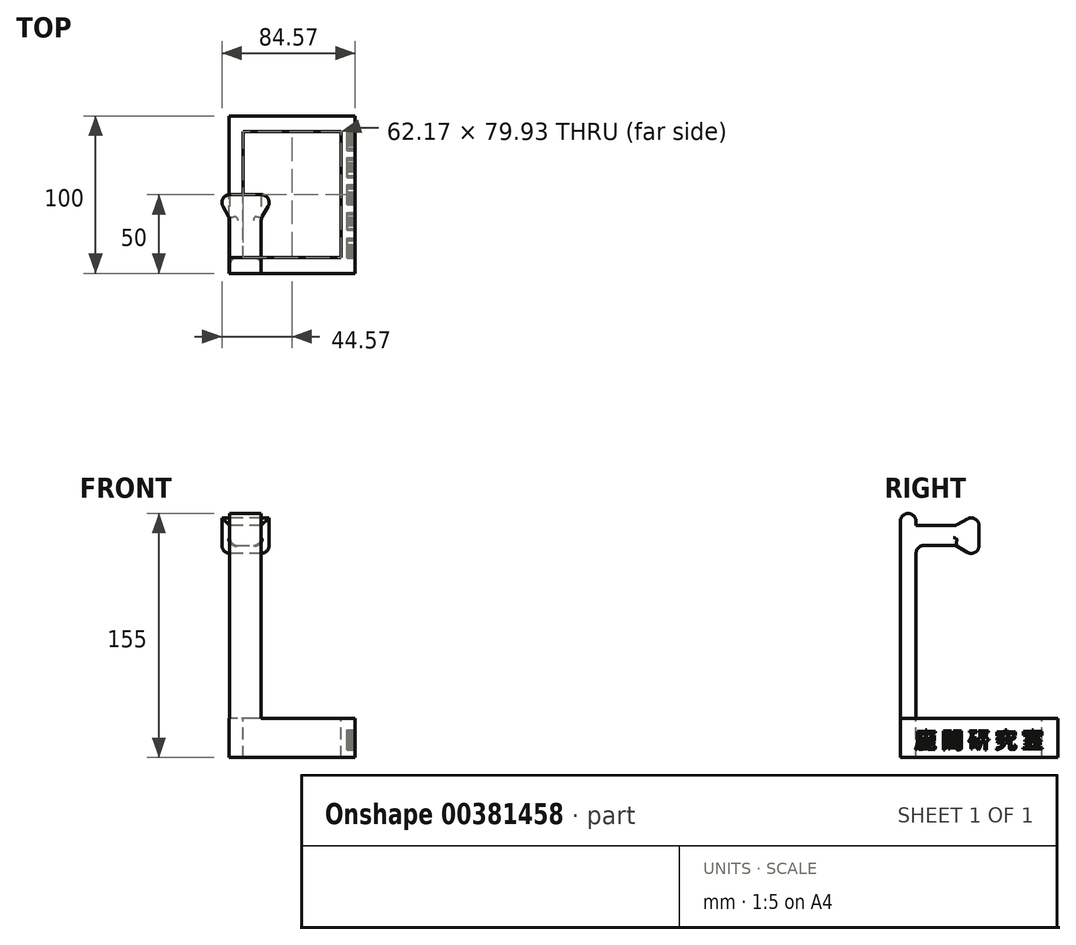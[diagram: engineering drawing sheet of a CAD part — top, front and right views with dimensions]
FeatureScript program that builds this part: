
annotation { "Feature Type Name" : "Feature", "Feature Type Description" : "" }
export const myFeature = defineFeature(function(context is Context, id is Id, definition is map)
    precondition{}
    {
        {
            var Q0;
            Q0=qCreatedBy(makeId("Top.planeOp"),FACE);
            var sketch = newSketch(context, id + "F0", { "sketchPlane" : qUnion([Q0])});
            skLineSegment(sketch, "E0.bottom", {"start": v(40, -50) * mm, "end": v(-40, -50) * mm});
            skLineSegment(sketch, "E0.top", {"start": v(40, 50) * mm, "end": v(-40, 50) * mm});
            skLineSegment(sketch, "E0.left", {"start": v(40, -50) * mm, "end": v(40, 50) * mm});
            skLineSegment(sketch, "E0.right", {"start": v(-40, -50) * mm, "end": v(-40, 50) * mm});
            skPoint(sketch, "E0.middle", {"position": v(0, 0) * mm});
            skSolve(sketch);
        }
        {
            var Q0;
            Q0=makeQuery(id+"F0.imprint","IMPRINT",FACE,{"disambiguationData":[TD([[makeQuery(id+"F0.imprint","IMPRINT",EDGE,{"derivedFrom":sQuery(id+"F0.wireOp",EDGE,"E0.bottom")}),-1.0]])]});
            extrude(context, id + "F1", {"entities" : qUnion([Q0]), "depth" : 25 * mm});
        }
        {
            var Q0;
            Q0=makeQuery(id+"F1.opExtrude","CAP_FACE",FACE,{"disambiguationData":[OSD([sQuery(id+"F0.wireOp",EDGE,"E0.bottom"),sQuery(id+"F0.wireOp",EDGE,"E0.top"),sQuery(id+"F0.wireOp",EDGE,"E0.left"),sQuery(id+"F0.wireOp",EDGE,"E0.right")])],"isStart":false});
            var sketch = newSketch(context, id + "F2", { "sketchPlane" : qUnion([Q0])});
            skLineSegment(sketch, "E1.bottom", {"start": v(-19.57, -50) * mm, "end": v(-39.57, -50) * mm});
            skLineSegment(sketch, "E1.top", {"start": v(-19.57, -40) * mm, "end": v(-39.57, -40) * mm});
            skLineSegment(sketch, "E1.left", {"start": v(-19.57, -50) * mm, "end": v(-19.57, -40) * mm});
            skLineSegment(sketch, "E1.right", {"start": v(-39.57, -50) * mm, "end": v(-39.57, -40) * mm});
            skPoint(sketch, "E1.middle", {"position": v(-29.57, -45) * mm});
            skSolve(sketch);
        }
        {
            var Q0;
            Q0=makeQuery(id+"F2.imprint","IMPRINT",FACE,{"disambiguationData":[TD([[makeQuery(id+"F2.imprint","IMPRINT",EDGE,{"derivedFrom":sQuery(id+"F2.wireOp",EDGE,"E1.bottom")}),-1.0]])]});
            extrude(context, id + "F3", {"entities" : qUnion([Q0]), "operationType" : NewBodyOperationType.ADD, "depth" : 130 * mm});
        }
        {
            var Q0;
            Q0=makeQuery(id+"F1.opExtrude","SWEPT_FACE",FACE,{"disambiguationData":[OSD([sQuery(id+"F0.wireOp",EDGE,"E0.left")])]});
            var sketch = newSketch(context, id + "F4", { "sketchPlane" : qUnion([Q0])});
            skText(sketch, "E2", { "text": "鹿 間 研 究 室", "fontName": "NotoSansCJKjp-Regular.otf"});
            const initialGuessF4  = {"E2": [-0.04089, 0.006, 1, 0, 0.01]};
            skSetInitialGuess(sketch, initialGuessF4);
            skSolve(sketch);
        }
        {
            var Q0;
            Q0 = qSketchRegion(id + "F4", true);
            extrude(context, id + "F5", {"entities" : qUnion([Q0]), "operationType" : NewBodyOperationType.REMOVE, "oppositeDirection" : true, "depth" : 5 * mm});
        }
        {
            var Q0;
            Q0=makeQuery(id+"F2.imprint","IMPRINT",FACE,{"disambiguationData":[TD([[makeQuery(id+"F2.imprint","IMPRINT",EDGE,{"derivedFrom":sQuery(id+"F2.wireOp",EDGE,"E1.top")}),-1.0]])]});
            var sketch = newSketch(context, id + "F6", { "sketchPlane" : qUnion([Q0])});
            skLineSegment(sketch, "E3.bottom", {"start": v(31.09, -39.97) * mm, "end": v(-31.09, -39.97) * mm});
            skLineSegment(sketch, "E3.top", {"start": v(31.09, 39.97) * mm, "end": v(-31.09, 39.97) * mm});
            skLineSegment(sketch, "E3.left", {"start": v(31.09, -39.97) * mm, "end": v(31.09, 39.97) * mm});
            skLineSegment(sketch, "E3.right", {"start": v(-31.09, -39.97) * mm, "end": v(-31.09, 39.97) * mm});
            skPoint(sketch, "E3.middle", {"position": v(0, 0) * mm});
            skSolve(sketch);
        }
        {
            var Q0;
            Q0 = qSketchRegion(id + "F6", true);
            extrude(context, id + "F7", {"entities" : qUnion([Q0]), "operationType" : NewBodyOperationType.REMOVE, "endBound" : BoundingType.THROUGH_ALL, "oppositeDirection" : true, "depth" : 25 * mm});
        }
        {
            var Q0;
            Q0=makeQuery(id+"F3.opExtrude","SWEPT_FACE",FACE,{"disambiguationData":[OSD([sQuery(id+"F2.wireOp",EDGE,"E1.top")])]});
            var sketch = newSketch(context, id + "F8", { "sketchPlane" : qUnion([Q0])});
            skLineSegment(sketch, "E4.bottom", {"start": v(19.57, 147.26) * mm, "end": v(39.57, 147.26) * mm});
            skLineSegment(sketch, "E4.top", {"start": v(19.57, 134.68) * mm, "end": v(39.57, 134.68) * mm});
            skLineSegment(sketch, "E4.left", {"start": v(19.57, 147.26) * mm, "end": v(19.57, 134.68) * mm});
            skLineSegment(sketch, "E4.right", {"start": v(39.57, 147.26) * mm, "end": v(39.57, 134.68) * mm});
            skSolve(sketch);
        }
        {
            var Q0;
            Q0=makeQuery(id+"F8.imprint","IMPRINT",FACE,{"disambiguationData":[TD([[makeQuery(id+"F8.imprint","IMPRINT",EDGE,{"derivedFrom":sQuery(id+"F8.wireOp",EDGE,"E4.bottom")}),-1.0]])]});
            extrude(context, id + "F9", {"entities" : qUnion([Q0]), "operationType" : NewBodyOperationType.ADD, "depth" : 25 * mm});
        }
        {
            var Q0;
            Q0=makeQuery(id+"F9.opExtrude","CAP_FACE",FACE,{"disambiguationData":[OSD([sQuery(id+"F8.wireOp",EDGE,"E4.bottom"),sQuery(id+"F8.wireOp",EDGE,"E4.top"),sQuery(id+"F8.wireOp",EDGE,"E4.left"),sQuery(id+"F8.wireOp",EDGE,"E4.right")])],"isStart":false});
            extrude(context, id + "F10", {"entities" : qUnion([Q0]), "operationType" : NewBodyOperationType.ADD, "depth" : 10 * mm, "hasDraft" : true, "draftAngle" : 30 * degree});
        }
        {
            var Q0;
            Q0=makeQuery(id+"F10.opExtrude","CAP_FACE",FACE,{"disambiguationData":[OSD([sQuery(id+"F8.wireOp",EDGE,"E4.bottom"),sQuery(id+"F8.wireOp",EDGE,"E4.top"),sQuery(id+"F8.wireOp",EDGE,"E4.left"),sQuery(id+"F8.wireOp",EDGE,"E4.right")])],"isStart":false});
            extrude(context, id + "F11", {"entities" : qUnion([Q0]), "operationType" : NewBodyOperationType.ADD, "depth" : 5 * mm});
        }
        {
            var Q0;
            Q0=makeQuery(id+"F11.opExtrude","CAP_FACE",FACE,{"disambiguationData":[OSD([sQuery(id+"F8.wireOp",EDGE,"E4.bottom"),sQuery(id+"F8.wireOp",EDGE,"E4.top"),sQuery(id+"F8.wireOp",EDGE,"E4.left"),sQuery(id+"F8.wireOp",EDGE,"E4.right")])],"isStart":false});
            fillet(context, id + "F12", {"entities" : qUnion([Q0]), "radius" : 5 * mm, "tangentPropagation" : true, "allowEdgeOverflow" : false});
        }
        {
            var Q0;
            {var subQ0=sQuery(id+"F8.wireOp",EDGE,"E4.bottom");Q0=makeQuery(id+"F10.boolean.opBoolean","MERGE",EDGE,{"derivedFrom":[makeQuery(id+"F9.opExtrude","CAP_EDGE",EDGE,{"disambiguationData":[OSD([subQ0])],"isStart":false}),makeQuery(id+"F10.opExtrude","CAP_EDGE",EDGE,{"disambiguationData":[OSD([subQ0])],"isStart":true})]});}
            var Q1;
            {var subQ0=sQuery(id+"F8.wireOp",EDGE,"E4.left");Q1=makeQuery(id+"F10.boolean.opBoolean","MERGE",EDGE,{"derivedFrom":[makeQuery(id+"F9.opExtrude","CAP_EDGE",EDGE,{"disambiguationData":[OSD([subQ0])],"isStart":false}),makeQuery(id+"F10.opExtrude","CAP_EDGE",EDGE,{"disambiguationData":[OSD([subQ0])],"isStart":true})]});}
            var Q2;
            {var subQ0=sQuery(id+"F8.wireOp",EDGE,"E4.top");Q2=makeQuery(id+"F10.boolean.opBoolean","MERGE",EDGE,{"derivedFrom":[makeQuery(id+"F9.opExtrude","CAP_EDGE",EDGE,{"disambiguationData":[OSD([subQ0])],"isStart":false}),makeQuery(id+"F10.opExtrude","CAP_EDGE",EDGE,{"disambiguationData":[OSD([subQ0])],"isStart":true})]});}
            var Q3;
            {var subQ0=sQuery(id+"F8.wireOp",EDGE,"E4.right");Q3=makeQuery(id+"F10.boolean.opBoolean","MERGE",EDGE,{"derivedFrom":[makeQuery(id+"F9.opExtrude","CAP_EDGE",EDGE,{"disambiguationData":[OSD([subQ0])],"isStart":false}),makeQuery(id+"F10.opExtrude","CAP_EDGE",EDGE,{"disambiguationData":[OSD([subQ0])],"isStart":true})]});}
            var Q4;
            Q4=makeQuery(id+"F9.opExtrude","CAP_EDGE",EDGE,{"disambiguationData":[OSD([sQuery(id+"F8.wireOp",EDGE,"E4.bottom")])],"isStart":true});
            var Q5;
            Q5=makeQuery(id+"F9.opExtrude","CAP_EDGE",EDGE,{"disambiguationData":[OSD([sQuery(id+"F8.wireOp",EDGE,"E4.top")])],"isStart":true});
            var Q6;
            Q6=makeQuery(id+"F3.opExtrude","CAP_EDGE",EDGE,{"disambiguationData":[OSD([sQuery(id+"F2.wireOp",EDGE,"E1.top")])],"isStart":false});
            var Q7;
            Q7=makeQuery(id+"F3.opExtrude","CAP_EDGE",EDGE,{"disambiguationData":[OSD([sQuery(id+"F2.wireOp",EDGE,"E1.bottom")])],"isStart":false});
            var Q8;
            {var subQ0=sQuery(id+"F8.wireOp",EDGE,"E4.bottom");Q8=makeQuery(id+"F12.opFillet","BLEND_EDGE",EDGE,{"blendedFrom":[makeQuery(id+"F11.opExtrude","CAP_EDGE",EDGE,{"disambiguationData":[OSD([subQ0])],"isStart":false}),makeQuery(id+"F10.opExtrude","SWEPT_FACE",FACE,{"disambiguationData":[OSD([subQ0])]})],"blendedInto":[makeQuery(id+"F10.opExtrude","SWEPT_FACE",FACE,{"disambiguationData":[OSD([subQ0])]})]});}
            var Q9;
            {var subQ0=sQuery(id+"F8.wireOp",EDGE,"E4.top");Q9=makeQuery(id+"F12.opFillet","BLEND_EDGE",EDGE,{"blendedFrom":[makeQuery(id+"F11.opExtrude","CAP_EDGE",EDGE,{"disambiguationData":[OSD([subQ0])],"isStart":false}),makeQuery(id+"F10.opExtrude","SWEPT_FACE",FACE,{"disambiguationData":[OSD([subQ0])]})],"blendedInto":[makeQuery(id+"F10.opExtrude","SWEPT_FACE",FACE,{"disambiguationData":[OSD([subQ0])]})]});}
            fillet(context, id + "F13", {"entities" : qUnion([Q0, Q1, Q2, Q3, Q4, Q5, Q6, Q7, Q8, Q9]), "radius" : 5 * mm, "tangentPropagation" : true, "allowEdgeOverflow" : false});
        }
        {
            var Q0;
            {var subQ0=sQuery(id+"F2.wireOp",EDGE,"E1.right");var subQ1=sQuery(id+"F2.wireOp",EDGE,"E1.top");Q0=makeQuery(id+"F9.boolean.opBoolean","SPLIT",EDGE,{"disambiguationData":[TD([makeQuery(id+"F9.opExtrude","SWEPT_FACE",FACE,{"disambiguationData":[OSD([sQuery(id+"F8.wireOp",EDGE,"E4.top")])]})])],"derivedFrom":makeQuery(id+"F3.opExtrude","SWEPT_EDGE",EDGE,{"disambiguationData":[OSD([subQ1,subQ0])]})});}
            var Q1;
            Q1=makeQuery(id+"F13.opFillet","BLEND_EDGE",EDGE,{"blendedFrom":[makeQuery(id+"F9.opExtrude","CAP_EDGE",EDGE,{"disambiguationData":[OSD([sQuery(id+"F8.wireOp",EDGE,"E4.bottom")])],"isStart":true}),makeQuery(id+"F9.boolean.opBoolean","MERGE",FACE,{"derivedFrom":[makeQuery(id+"F3.opExtrude","SWEPT_FACE",FACE,{"disambiguationData":[OSD([sQuery(id+"F2.wireOp",EDGE,"E1.right")])]}),makeQuery(id+"F9.opExtrude","SWEPT_FACE",FACE,{"disambiguationData":[OSD([sQuery(id+"F8.wireOp",EDGE,"E4.right")])]})]})],"blendedInto":[makeQuery(id+"F9.boolean.opBoolean","MERGE",FACE,{"derivedFrom":[makeQuery(id+"F3.opExtrude","SWEPT_FACE",FACE,{"disambiguationData":[OSD([sQuery(id+"F2.wireOp",EDGE,"E1.right")])]}),makeQuery(id+"F9.opExtrude","SWEPT_FACE",FACE,{"disambiguationData":[OSD([sQuery(id+"F8.wireOp",EDGE,"E4.right")])]})]})]});
            var Q2;
            Q2=makeQuery(id+"F13.opFillet","BLEND_EDGE",EDGE,{"blendedFrom":[makeQuery(id+"F9.opExtrude","CAP_EDGE",EDGE,{"disambiguationData":[OSD([sQuery(id+"F8.wireOp",EDGE,"E4.bottom")])],"isStart":true}),makeQuery(id+"F9.boolean.opBoolean","MERGE",FACE,{"derivedFrom":[makeQuery(id+"F3.opExtrude","SWEPT_FACE",FACE,{"disambiguationData":[OSD([sQuery(id+"F2.wireOp",EDGE,"E1.left")])]}),makeQuery(id+"F9.opExtrude","SWEPT_FACE",FACE,{"disambiguationData":[OSD([sQuery(id+"F8.wireOp",EDGE,"E4.left")])]})]})],"blendedInto":[makeQuery(id+"F9.boolean.opBoolean","MERGE",FACE,{"derivedFrom":[makeQuery(id+"F3.opExtrude","SWEPT_FACE",FACE,{"disambiguationData":[OSD([sQuery(id+"F2.wireOp",EDGE,"E1.left")])]}),makeQuery(id+"F9.opExtrude","SWEPT_FACE",FACE,{"disambiguationData":[OSD([sQuery(id+"F8.wireOp",EDGE,"E4.left")])]})]})]});
            var Q3;
            {var subQ0=sQuery(id+"F2.wireOp",EDGE,"E1.top");var subQ1=sQuery(id+"F2.wireOp",EDGE,"E1.left");Q3=makeQuery(id+"F9.boolean.opBoolean","SPLIT",EDGE,{"disambiguationData":[TD([makeQuery(id+"F9.opExtrude","SWEPT_FACE",FACE,{"disambiguationData":[OSD([sQuery(id+"F8.wireOp",EDGE,"E4.top")])]})])],"derivedFrom":makeQuery(id+"F3.opExtrude","SWEPT_EDGE",EDGE,{"disambiguationData":[OSD([subQ0,subQ1])]})});}
            fillet(context, id + "F14", {"entities" : qUnion([Q0, Q1, Q2, Q3]), "radius" : 5 * mm, "tangentPropagation" : true, "allowEdgeOverflow" : false});
        }
    });
